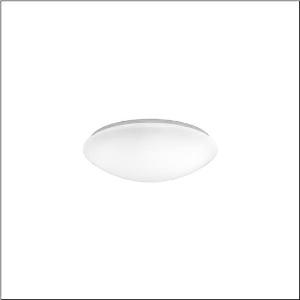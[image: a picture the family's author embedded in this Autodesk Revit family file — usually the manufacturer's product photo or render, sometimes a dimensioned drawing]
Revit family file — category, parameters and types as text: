
# Revit family: round_31_b_5pja032001a
name_source: partatom
category: Lighting Fixtures
units: mm (PartAtom-declared; Revit-internal decimal feet)

## family parameters
Cut with Voids When Loaded = No
Host = Face
Light Source = No
Part Type = Normal
Room Calculation Point = No
Round Connector Dimension = Use Diameter
Shared = No

## types (1)
- Round 31 B (1 x LED, 1900 lm, 15 W, 4000K)
    Apparent Load = 15 VA
    CIE Flux Codes = 42 71 89 88 100
    Color Rendering = 80
    Color Temperature = 4000K
    Default Elevation = 1800 mm
    Description = Round 31 B, wall and ceiling luminaire, primary optical cover: enclosure, of PMMA, light emission: direct distribution, primary light characteristic: symmetric, installation type: surface-mounted, LED, rated luminous flux: 1.900lm, luminous efficacy: 126lm/W, light colour: 840, colour temperature: 4000K, with terminal, 3+2-pole, max. 2.5mm², mains connection: 230V, AC, 50/60Hz, rated input power: 15W, luminaire housing, round, of steel, white, diameter: 290mm, height: 85mm, protection rating (complete): IP40, insulation class (complete): insulation class I (protective earthing), certification: CE, impact resistance: IK02, packaging unit: 1 piece
    Height = 85 mm
    Lamp = 1 x LED
    Lamp Light Flux = 1900 lm
    Lamp Power = 15 W
    Lamp count = 1
    Length = 290 mm
    Luminous efficacy = 127 lm/W
    Manufacturer = Siteco
    ModVariant = No
    Model = 5PJA032001A
    Mounting Place = Ceiling
    Mounting Type = Surface mounted
    Number of Poles = 1
    OnlyDefault = Yes
    Power Factor = 1
    Product Name = Round 31 B
    Product group = wall and ceiling luminaire
    ProductGroupID = 301
    Protection Class = Protection class I
    Protection Degree = IP 40
    RLX_Detail_Level = 1
    RLX_Emergency_Light_Flux = 0 lm
    RLX_Emergency_Type = 0
    RLX_Emergency_Type_DB = No
    RlxData = <blob elided: 9185 chars, md5=7c06847f>
    Socket = socket
    Standby Power = 0 W
    System Light Flux = 1900 lm
    System Power = 15 W
    Type Comments = Product without accessories
    Type Image = l_1258346.jpg
    URL = http://relux.com
    VarID = ---
    Voltage = 0 V
    Weight = 0.00 kg
    Width = 0 mm  [stored 0 ft]

note: [stored X ft] marks values corroborated as IEEE doubles in the binary element streams (Revit-internal decimal feet)

## geometry (parser evidence)
native form markers: Sweep x15
no freeform markers — native parametric forms only
